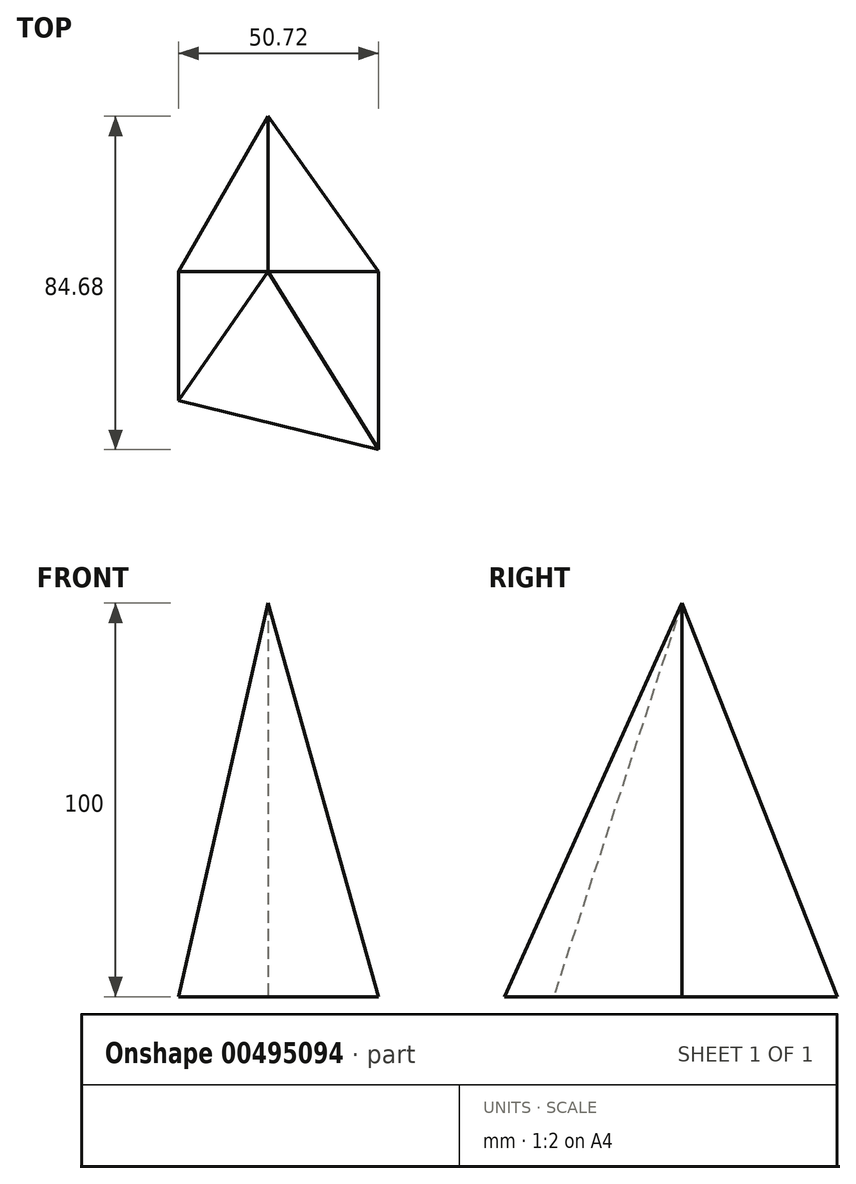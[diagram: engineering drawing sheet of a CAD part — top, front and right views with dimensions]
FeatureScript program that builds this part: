
annotation { "Feature Type Name" : "Feature", "Feature Type Description" : "" }
export const myFeature = defineFeature(function(context is Context, id is Id, definition is map)
    precondition{}
    {
        {
            var Q0;
            Q0=qCreatedBy(makeId("Top.planeOp"),FACE);
            var sketch = newSketch(context, id + "F0", { "sketchPlane" : qUnion([Q0])});
            skLineSegment(sketch, "E0", {"start": v(0, 39.5) * mm, "end": v(-22.74, 0) * mm});
            skLineSegment(sketch, "E1", {"start": v(-22.74, 0) * mm, "end": v(-22.74, -32.67) * mm});
            skLineSegment(sketch, "E2", {"start": v(0, 39.5) * mm, "end": v(27.98, 0) * mm});
            skLineSegment(sketch, "E3", {"start": v(27.98, 0) * mm, "end": v(27.98, -45.2) * mm});
            skLineSegment(sketch, "E4", {"start": v(-22.74, -32.67) * mm, "end": v(27.98, -45.2) * mm});
            skSolve(sketch);
        }
        {
            var Q0;
            Q0=qCreatedBy(makeId("Top.planeOp"),FACE);
            cPlane(context, id + "F1", {"entities" : qUnion([Q0]), "cplaneType" : CPlaneType.OFFSET, "offset" : 100 * mm, "width" : 152.4 * mm, "height" : 152.4 * mm});
        }
        {
            var Q0;
            Q0=qCreatedBy(id+"F1.planeOp",FACE);
            var sketch = newSketch(context, id + "F2", { "sketchPlane" : qUnion([Q0])});
            skPoint(sketch, "E5", {"position": v(0, 0) * mm});
            skSolve(sketch);
        }
        {
            var Q0;
            Q0=sQuery(id+"F2.wireOp",VERTEX,"E5");
            var Q1;
            Q1=makeQuery(id+"F0.imprint","IMPRINT",FACE,{"disambiguationData":[TD([[makeQuery(id+"F0.imprint","IMPRINT",EDGE,{"derivedFrom":sQuery(id+"F0.wireOp",EDGE,"E0")}),1.0]])]});
            loft(context, id + "F3", {"sheetProfilesArray" : [{ "sheetProfileEntities" : qUnion([Q0]) }, { "sheetProfileEntities" : qUnion([Q1]) }]});
        }
    });
